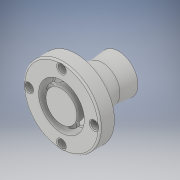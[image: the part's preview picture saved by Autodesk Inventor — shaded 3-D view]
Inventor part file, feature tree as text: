
AUTODESK INVENTOR PART (.ipt)
format: ipt  version: 2019 (Build 230136000, 136)  size: 260,096 bytes
history: native  units: mm
features: fillet x4, sketch x3, extrude x2, revolve x1
ambient origin geometry x8: Origin, YZ Plane, XZ Plane, XY Plane, X Axis, Y Axis, Z Axis, Center Point
bodies: Solid1 (feature_tree)
feature tree (10):
  extrude  "Extrusion1"  Depth=28.0mm
  extrude  "Extrusion2"  Depth=5.0mm
  revolve  "Revolution1"  [1 undecoded]
  fillet  "Fillet1"  Radius=47.0mm
  fillet  "Fillet2"  Radius=5.0mm
  fillet  "Fillet3"  Radius=4.0mm
  fillet  "Fillet4"  Radius=20.0mm
  sketch  "Sketch1"  dims[d0=19.0mm d1=28.0mm]
  sketch  "Sketch2"  dims[d2=5.0mm d3=5.0mm]
  sketch  "Sketch3"  dims[d4=5.0mm d5=5.0mm d7=47.0mm d8=5.0mm d9=0.0mm d10=4.0mm d11=0.0mm d12=20.0mm d21=90.0deg d23=1.0mm d24=28.0mm d25=4.0mm d26=47.0mm d27=0.5mm d28=1.0mm d29=16.580628mm d30=10.0mm d31=1.0mm d32=2.0mm]
note: 1 required parameter value undecoded (feature->parameter linkage not recoverable at this tier; creation-order binding heuristic only, values carry confidence <= 0.55)
